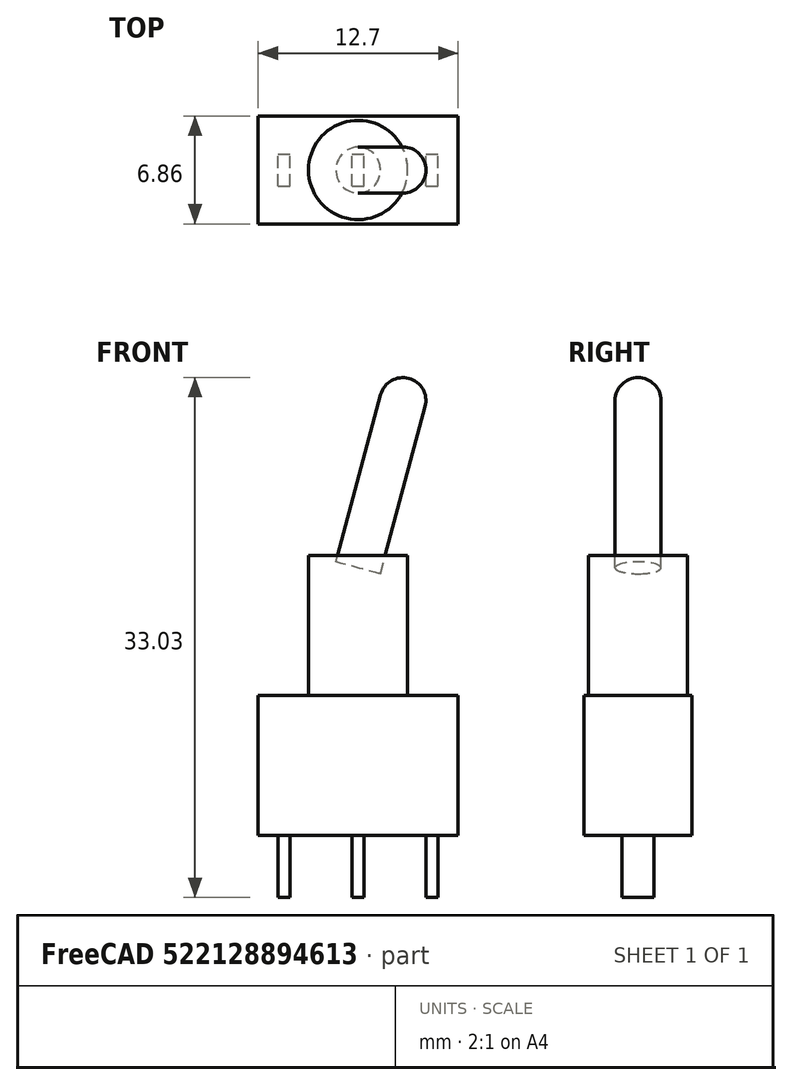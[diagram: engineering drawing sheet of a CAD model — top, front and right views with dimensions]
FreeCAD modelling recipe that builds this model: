
FCSTD DOCUMENT  (FreeCAD 0.19R)
Label: switch_CK
License: All rights reserved
LicenseURL: http://en.wikipedia.org/wiki/All_rights_reserved
objects: Part::Box×4, Part::Cylinder×2, Part::Sphere×1, Part::MultiFuse×1
note: 8 computed .brp shape members not serialized (recipe doc carries the construction recipe); baked Part::Feature solids carry a one-line shape summary decoded from their .brp

FEATURE [Part::Box] Box  label="Cube"
  AttacherType = Attacher::AttachEngine3D
  Height = 8.89
  Length = 12.7
  Placement = pos=(-6.35,-3.43,0) rot=(0,0,1;0rad)
  Width = 6.86
FEATURE [Part::Cylinder] Cylinder
  Angle = 360
  AttacherType = Attacher::AttachEngine3D
  Height = 8.89
  Placement = pos=(0,0,8.89) rot=(0,0,1;0rad)
  Radius = 3.15
FEATURE [Part::Box] Box001  label="Cube001"
  AttacherType = Attacher::AttachEngine3D
  Height = 3.94
  Length = 0.76
  Placement = pos=(4.32,-1.015,-3.94) rot=(0,0,1;0rad)
  Width = 2.03
FEATURE [Part::Box] Box002  label="Cube002"
  AttacherType = Attacher::AttachEngine3D
  Height = 3.94
  Length = 0.76
  Placement = pos=(-0.38,-1.015,-3.94) rot=(0,0,1;0rad)
  Width = 2.03
FEATURE [Part::Box] Box003  label="Cube003"
  AttacherType = Attacher::AttachEngine3D
  Height = 3.94
  Length = 0.76
  Placement = pos=(-5.08,-1.015,-3.94) rot=(0,0,1;0rad)
  Width = 2.03
FEATURE [Part::Cylinder] Cylinder001
  Angle = 360
  AttacherType = Attacher::AttachEngine3D
  Height = 11
  Radius = 1.46
FEATURE [Part::Sphere] Sphere
  Angle1 = -90
  Angle2 = 90
  Angle3 = 360
  AttacherType = Attacher::AttachEngine3D
  Placement = pos=(0,0,11) rot=(0,0,1;0rad)
  Radius = 1.46
FEATURE [Part::MultiFuse] Fusion
  Placement = pos=(0,0,17) rot=(0,1,0;0.261799rad)
  Shapes = -> [Cylinder001,Sphere]
